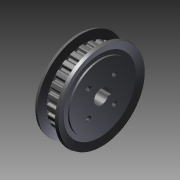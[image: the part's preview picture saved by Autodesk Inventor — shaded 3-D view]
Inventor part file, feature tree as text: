
AUTODESK INVENTOR PART (.ipt)
format: ipt  version: 2011 SP1 (Build 150282100, 282)  size: 552,448 bytes
history: native  units: mm
features: other x14, revolve x3, hole x2, extrude x2, thread x2, sketch x2, pattern_linear x1
ambient origin geometry x8: Origin, YZ Plane, XZ Plane, XY Plane, X Axis, Y Axis, Z Axis, Center Point
bodies: Solid1 (feature_tree)
feature tree (26):
  revolve  "Revolution1"  [1 undecoded]
  hole  "Hole1"  [1 undecoded]
  extrude  "Extrusion1"  TaperAngle=360.0deg  [1 undecoded]
  extrude  "Extrusion2"  Depth=14.56mm TaperAngle=0.0deg
  revolve  "Revolution2"  Angle=360.0deg
  thread  "Thread1"  [1 undecoded]
  revolve  "Revolution3"  [1 undecoded]
  thread  "Thread2"  [1 undecoded]
  hole  "Hole2"  [1 undecoded]
  pattern_linear  "Rectangular Pattern1"  [2 undecoded]
  other  "to_screw1_XY"
  other  "to_screw1_YZ"
  other  "to_screw1_ZX"
  other  "to_screw1_X"
  other  "to_screw1_Y"
  other  "to_screw1_Z"
  other  "to_screw1_Center"
  other  "to_screw2_XY"
  other  "to_screw2_YZ"
  other  "to_screw2_ZX"
  other  "to_screw2_X"
  other  "to_screw2_Y"
  other  "to_screw2_Z"
  other  "to_screw2_Center"
  sketch  "Sketch2"  dims[d0=360.0deg]
  sketch  "Sketch7"  dims[d1=8.0mm d2=6.0mm d3=4.0mm d4=2.0mm d5=90.0deg d6=12.5mm d7=0.0mm d8=7.5mm d9=0.0mm d10=12.5mm d11=0.0mm d12=360.0deg d13=14.56mm d14=0.0mm d15=360.0deg d16=15.96mm d17=0.0mm d18=2.459mm d19=6.2705mm d20=3.0mm d21=2.0mm d22=90.0deg d23=8.790148mm d24=120.0deg d25=20.0mm d27=14.142136mm d28=20.0mm d30=14.142136mm d31=0.0mm]
note: 9 required parameter values undecoded (feature->parameter linkage not recoverable at this tier; creation-order binding heuristic only, values carry confidence <= 0.55)